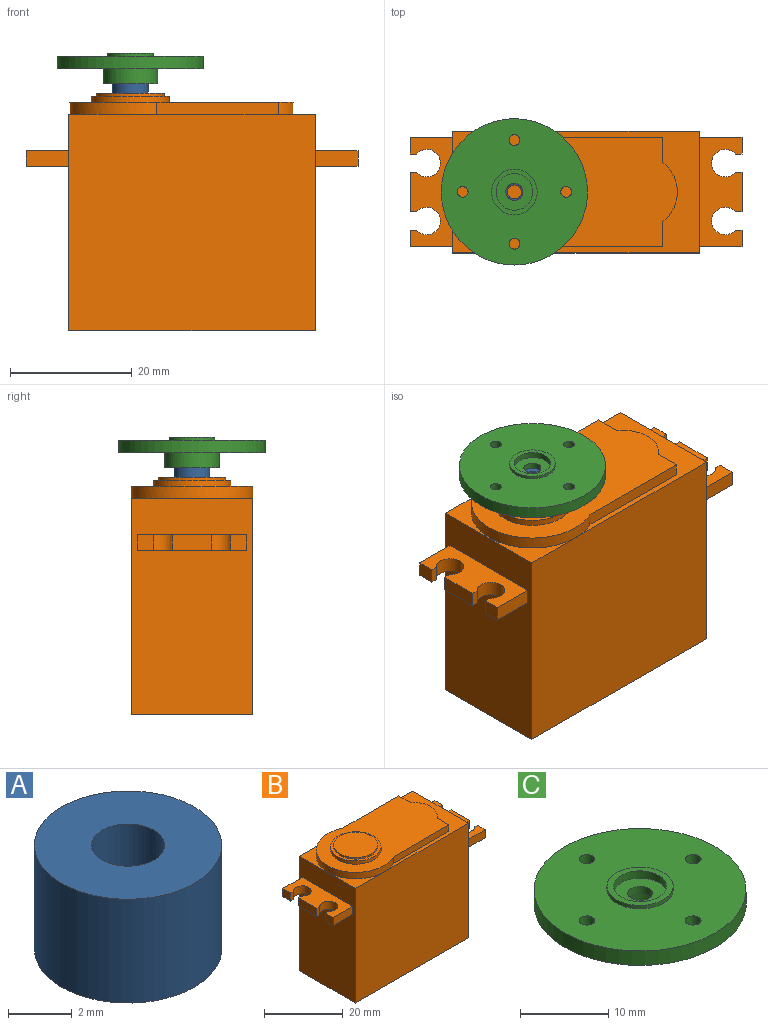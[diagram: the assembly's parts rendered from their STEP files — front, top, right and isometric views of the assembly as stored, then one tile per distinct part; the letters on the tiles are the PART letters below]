
ASSEMBLY  parts=3 mates=2
PART A: 4 faces, bbox 5.9x5.9x4 mm
  f0: plane 5.9x5.9mm, normal (0,0,1), area 23.2mm2, adj f2,f3
  f1: plane 5.9x5.9mm, normal (0,0,-1), area 23.2mm2, adj f2,f3
  f2: cylinder r=2.95mm len=5.9mm, axis (0,0,-1), area 74.1mm2, adj f0,f1
  f3: cylinder r=1.15mm len=4mm, axis (0,0,-1), area 28.9mm2, adj f0,f1
PART B: 44 faces, bbox 54.5x20x39 mm
  f0: plane 35.5x20mm, normal (-1,0,0), area 665mm2, adj f5,f6,f7,f8,f31,f32,f33,f39
  f1: plane 35.5x20mm, normal (1,0,0), area 665mm2, adj f4,f6,f7,f8,f18,f24,f25,f38
  f2: plane 12.8x12.8mm, normal (0,0,1), area 31mm2, adj f15,f16
  f3: plane 36.76x20mm, normal (0,0,1), area 488.8mm2, adj f9,f10,f11,f12,f13,f14,f15
  f4: plane 30.36x20mm, normal (0,0,1), area 146.7mm2, adj f1,f6,f7,f9,f10,f11,f12,f13
  f5: plane 20x10.14mm, normal (0,0,1), area 45.7mm2, adj f0,f6,f7,f9
  f6: plane 40.5x35.5mm, normal (0,-1,0), area 1437.8mm2, adj f0,f1,f4,f5,f8
  f7: plane 40.5x35.5mm, normal (0,1,0), area 1437.8mm2, adj f0,f1,f4,f5,f8
  f8: plane 40.5x20mm, normal (0,0,-1), area 810mm2, adj f0,f1,f6,f7
  f9: cylinder r=10mm len=20mm, axis (0,0,-1), area 80.9mm2, adj f3,f4,f5,f10,f14
  f10: plane 20x2mm, normal (0,-1,0), area 40mm2, adj f3,f4,f9,f11
  f11: plane 4.2x2mm, normal (1,0,0), area 8.4mm2, adj f3,f4,f10,f12
  f12: cylinder r=6mm len=9.6mm, axis (0,0,-1), area 22.3mm2, adj f3,f4,f11,f13
  f13: plane 4.2x2mm, normal (1,0,0), area 8.4mm2, adj f3,f4,f12,f14
  f14: plane 20x2mm, normal (0,1,0), area 40mm2, adj f3,f4,f9,f13
  f15: cylinder r=6.4mm len=12.8mm, axis (0,0,-1), area 40.2mm2, adj f2,f3
  f16: cylinder r=5.58mm len=11.15mm, axis (0,0,-1), area 17.5mm2, adj f2,f17
  f17: plane 11.15x11.15mm, normal (0,0,1), area 97.6mm2, adj f16
  f18: plane 7x2.5mm, normal (0,1,0), area 17.5mm2, adj f1,f19,f24,f25
  f19: plane 2.75x2.5mm, normal (1,0,0), area 6.9mm2, adj f18,f20,f24,f25
  f20: plane 2.5x1.07mm, normal (0,-1,0), area 2.7mm2, adj f19,f21,f24,f25
  f21: cylinder r=2.25mm len=4.5mm, axis (0,0,1), area 27.1mm2, adj f20,f22,f24,f25
  f22: plane 2.5x1.07mm, normal (0,1,0), area 2.7mm2, adj f21,f23,f24,f25
  f23: plane 6.5x2.5mm, normal (1,0,0), area 16.2mm2, adj f22,f24,f25,f34
  f24: plane 18x7mm, normal (0,0,-1), area 90.1mm2, adj f1,f18,f19,f20,f21,f22,f23,f34
  f25: plane 18x7mm, normal (0,0,1), area 90.1mm2, adj f1,f18,f19,f20,f21,f22,f23,f34
  f26: plane 6.5x2.5mm, normal (-1,0,0), area 16.2mm2, adj f27,f32,f33,f43
  f27: plane 2.5x1.07mm, normal (0,1,0), area 2.7mm2, adj f26,f28,f32,f33
  f28: cylinder r=2.25mm len=4.5mm, axis (0,0,1), area 27.1mm2, adj f27,f29,f32,f33
  f29: plane 2.5x1.07mm, normal (0,-1,0), area 2.7mm2, adj f28,f30,f32,f33
  f30: plane 2.75x2.5mm, normal (-1,0,0), area 6.9mm2, adj f29,f31,f32,f33
  f31: plane 7x2.5mm, normal (0,1,0), area 17.5mm2, adj f0,f30,f32,f33
  f32: plane 18x7mm, normal (0,0,-1), area 90.1mm2, adj f0,f26,f27,f28,f29,f30,f31,f39
  f33: plane 18x7mm, normal (0,0,1), area 90.1mm2, adj f0,f26,f27,f28,f29,f30,f31,f39
  f34: plane 2.5x1.07mm, normal (0,-1,0), area 2.7mm2, adj f23,f24,f25,f35
  f35: cylinder r=2.25mm len=4.5mm, axis (0,0,1), area 27.1mm2, adj f24,f25,f34,f36
  f36: plane 2.5x1.07mm, normal (0,1,0), area 2.7mm2, adj f24,f25,f35,f37
  f37: plane 2.75x2.5mm, normal (1,0,0), area 6.9mm2, adj f24,f25,f36,f38
  f38: plane 7x2.5mm, normal (0,-1,0), area 17.5mm2, adj f1,f24,f25,f37
  f39: plane 7x2.5mm, normal (0,-1,0), area 17.5mm2, adj f0,f32,f33,f40
  f40: plane 2.75x2.5mm, normal (-1,0,0), area 6.9mm2, adj f32,f33,f39,f41
  f41: plane 2.5x1.07mm, normal (0,1,0), area 2.7mm2, adj f32,f33,f40,f42
  f42: cylinder r=2.25mm len=4.5mm, axis (0,0,1), area 27.1mm2, adj f32,f33,f41,f43
  f43: plane 2.5x1.07mm, normal (0,-1,0), area 2.7mm2, adj f26,f32,f33,f42
PART C: 16 faces, bbox 24x24x5 mm
  f0: cylinder r=1.4mm len=2.8mm, axis (0,0,1), area 8.8mm2, adj f13,f15
  f1: cylinder r=12mm len=24mm, axis (0,0,1), area 150.8mm2, adj f2,f7
  f2: plane 24x24mm, normal (0,0,-1), area 378.8mm2, adj f1,f3,f8,f9,f10,f11
  f3: cylinder r=4.5mm len=9mm, axis (0,0,1), area 70.7mm2, adj f2,f4
  f4: plane 9x9mm, normal (0,0,-1), area 35.3mm2, adj f3,f14
  f5: plane 7.5x7.5mm, normal (0,0,1), area 15.9mm2, adj f6,f12
  f6: cylinder r=3.75mm len=7.5mm, axis (0,0,1), area 11.8mm2, adj f5,f7
  f7: plane 24x24mm, normal (0,0,1), area 398.3mm2, adj f1,f6,f8,f9,f10,f11
  f8: cylinder r=0.89mm len=2mm, axis (0,0,1), area 11.2mm2, adj f2,f7
  f9: cylinder r=0.89mm len=2mm, axis (0,0,1), area 11.2mm2, adj f2,f7
  f10: cylinder r=0.89mm len=2mm, axis (0,0,1), area 11.2mm2, adj f2,f7
  f11: cylinder r=0.89mm len=2mm, axis (0,0,1), area 11.2mm2, adj f2,f7
  f12: cylinder r=3mm len=6mm, axis (0,0,1), area 18.8mm2, adj f5,f13
  f13: plane 6x6mm, normal (0,0,1), area 22.1mm2, adj f0,f12
  f14: cylinder r=3mm len=6mm, axis (0,0,-1), area 56.5mm2, adj f4,f15
  f15: plane 6x6mm, normal (0,0,-1), area 22.1mm2, adj f0,f14
PLACE A t=(-26.13,-13.22,66.48)mm
PLACE B t=(-16.03,-13.22,27.48)mm
PLACE C t=(-26.13,-13.22,72.48)mm
MATE fastened C.f0 <-> A.f2  axis (0,0,-1) through (-26.13,-13.22,70.48)mm
MATE fastened A.f2 <-> B.f9  axis (0,0,-1) through (-26.13,-13.22,66.48)mm
